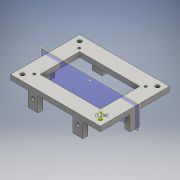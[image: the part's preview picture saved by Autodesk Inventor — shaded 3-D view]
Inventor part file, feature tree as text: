
AUTODESK INVENTOR PART (.ipt)
format: ipt  version: 2016 SP2 (Build 200236200, 236)  size: 270,336 bytes
history: native  units: mm
features: extrude x9, sketch x9, other x1, plane x1
ambient origin geometry x8: Origin, YZ Plane, XZ Plane, XY Plane, X Axis, Y Axis, Z Axis, Center Point
bodies: Solid1 (feature_tree)
feature tree (20):
  extrude  "Rim"  Depth=40.0mm
  extrude  "Pegs"  Depth=15.0mm
  extrude  "Nut Hexes"  Depth=5.0mm
  extrude  "Bolt Holes"  Depth=2.5mm
  other  "For Construction"
  extrude  "Attachment Points"  Depth=3.0mm
  extrude  "Connection Holes"  Depth=6.0mm
  extrude  "Legs 1"  Depth=3.0mm TaperAngle=0.0deg
  extrude  "Extrusion9"  Depth=5.0mm
  plane  "Work Plane2"
  extrude  "Extrusion10"  Depth=10.0mm TaperAngle=0.0deg
  sketch  "Sketch1"  dims[d0=61.0mm d1=40.0mm]
  sketch  "Sketch2"  dims[d2=15.0mm d3=15.0mm]
  sketch  "Sketch3"  dims[d4=5.0mm d5=0.0mm d6=67.4mm]
  sketch  "Sketch4"  dims[d7=45.53mm d8=2.5mm]
  sketch  "Sketch7"  dims[d9=3.0mm d10=0.0mm d11=3.175426mm d12=4.0mm]
  sketch  "Sketch9"  dims[d13=6.0mm d14=6.0mm]
  sketch  "Sketch10"  dims[d15=3.0mm d16=0.0mm d17=3.0mm d18=0.0mm]
  sketch  "Sketch11"  dims[d19=5.265587mm d20=5.0mm]
  sketch  "Sketch12"  dims[d21=10.0mm d22=10.0mm d23=0.0mm d26=3.0mm d27=0.0mm d28=5.0mm d29=10.0mm d30=5.0mm d31=10.0mm d32=15.0mm d33=0.0mm d34=5.0mm d35=0.0mm d36=3.175426mm d38=3.175426mm d40=3.0mm d41=0.0mm]
